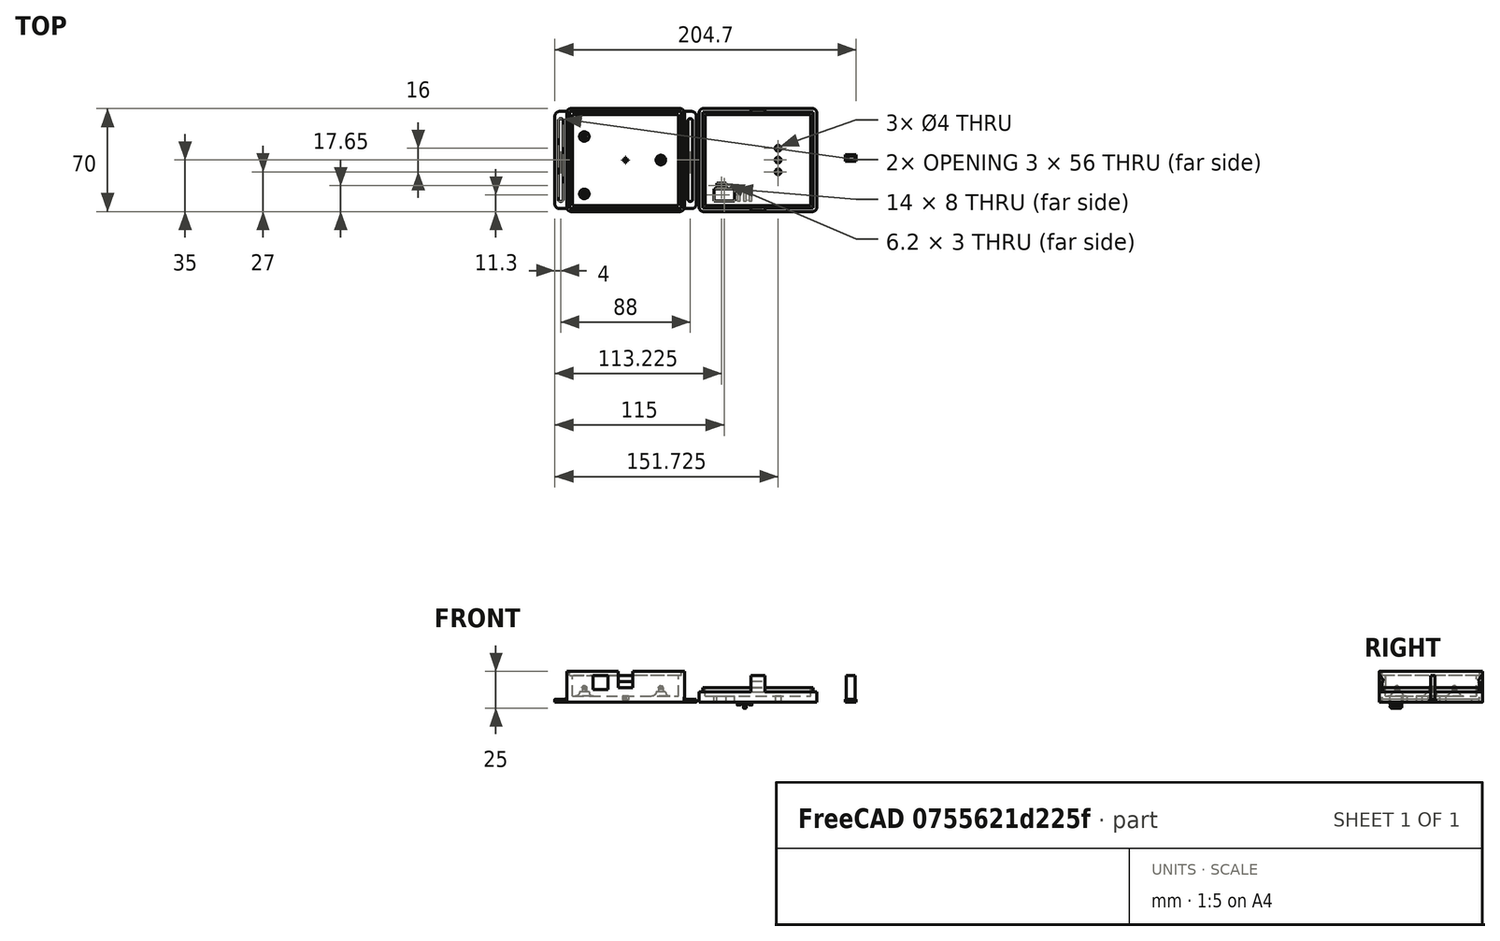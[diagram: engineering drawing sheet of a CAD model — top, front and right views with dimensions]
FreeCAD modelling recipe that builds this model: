
FCSTD DOCUMENT  (FreeCAD 1.0R39109 (Git))
Label: case
License: All rights reserved
LicenseURL: https://en.wikipedia.org/wiki/All_rights_reserved
objects: Sketcher::SketchObject×28, PartDesign::Pad×19, PartDesign::Body×12, PartDesign::Boolean×8, PartDesign::Fillet×6, PartDesign::Pocket×6, App::Link×3, App::FeaturePython×3, PartDesign::Revolution×3, PartDesign::Thickness×2, Assembly::JointGroup×1, Assembly::AssemblyObject×1, App::Part×1
note: 192 computed .brp shape members not serialized (recipe doc carries the construction recipe); baked Part::Feature solids carry a one-line shape summary decoded from their .brp

FEATURE [Sketcher::SketchObject] Sketch
  ArcFitTolerance = 1e-06
  AttachmentSupport = -> [XY_Plane001]
  FullyConstrained = true
  MakeInternals = false
  MapMode = 5
  sketch-geometry (4):
    g0: LineSegment StartX=-40 StartY=35 StartZ=0 EndX=-40 EndY=-35 EndZ=0
    g1: LineSegment StartX=-40 StartY=-35 StartZ=0 EndX=40 EndY=-35 EndZ=0
    g2: LineSegment StartX=40 StartY=-35 StartZ=0 EndX=40 EndY=35 EndZ=0
    g3: LineSegment StartX=40 StartY=35 StartZ=0 EndX=-40 EndY=35 EndZ=0
  constraints (10):
    c: Coincident(g0,g1)
    c: Coincident(g1,g2)
    c: Coincident(g2,g3)
    c: Coincident(g3,g0)
    c: Vertical(g2)
    c: Horizontal(g1)
    c: Symmetric(g0,g2,g-2)
    c: Symmetric(g0,g0,g-1)
    c: DistanceX(g3,g3) = 80
    c: DistanceY(g2,g2) = 70
FEATURE [PartDesign::Pad] Pad  label="case"
  Direction = (0,0,1)
  Length = 21
  Length2 = 10
  Profile = -> Sketch
  ReferenceAxis = -> Sketch [N_Axis]
  Refine = true
  Suppressed = false
  Type = 0
FEATURE [PartDesign::Thickness] Thickness  label="case_t"
  Base = -> Pad [Face6]
  BaseFeature = -> Pad
  Intersection = false
  Join = 0
  Mode = 0
  Refine = true
  Reversed = true
  SupportTransform = false
  Suppressed = false
  Value = 4
FEATURE [PartDesign::Fillet] Fillet
  Base = -> Thickness [Edge1,Edge2,Edge5,Edge8]
  BaseFeature = -> Thickness
  Radius = 3
  Refine = true
  SupportTransform = false
  Suppressed = false
  UseAllEdges = false
FEATURE [Sketcher::SketchObject] Sketch001  label="pcb_holders_s"
  ArcFitTolerance = 1e-06
  AttachmentSupport = -> [Fillet]
  FullyConstrained = true
  MakeInternals = false
  MapMode = 5
  Placement = pos=(0,0,4) rot=(0,0,1;0rad)
  sketch-geometry (7):
    g0: Circle CenterX=-28 CenterY=-23 CenterZ=0 NormalX=0 NormalY=0 NormalZ=1 AngleXU=0 Radius=3.25
    g1: Circle CenterX=-28 CenterY=16 CenterZ=0 NormalX=0 NormalY=0 NormalZ=1 AngleXU=0 Radius=3.25
    g2: Circle CenterX=24 CenterY=-1.1e-15 CenterZ=0 NormalX=0 NormalY=0 NormalZ=1 AngleXU=0 Radius=3.25
    g3: LineSegment [constr] StartX=-32 StartY=27 StartZ=0 EndX=-32 EndY=-27 EndZ=0
    g4: LineSegment [constr] StartX=-32 StartY=-27 StartZ=0 EndX=32 EndY=-27 EndZ=0
    g5: LineSegment [constr] StartX=32 StartY=-27 StartZ=0 EndX=32 EndY=27 EndZ=0
    g6: LineSegment [constr] StartX=32 StartY=27 StartZ=0 EndX=-32 EndY=27 EndZ=0
  constraints (19):
    c: Radius(g0) = 3.25
    c: Radius(g1) = 3.25
    c: Diameter(g2) = 6.5
    c: Coincident(g3,g4)
    c: Coincident(g4,g5)
    c: Coincident(g5,g6)
    c: Coincident(g6,g3)
    c: Vertical(g3)
    c: Horizontal(g6)
    c: DistanceX(g6,g6) = 64
    c: DistanceY(g3,g3) = 54
    c: Symmetric(g3,g4,g-2)
    c: Symmetric(g5,g4,g-1)
    c: Distance(g0,g4) = 4
    c: Distance(g0,g3) = 4
    c: Distance(g1,g3) = 4
    c: Distance(g1,g6) = 11
    c: Distance(g2,g5) = 8
    c: Distance(g2,g4) = 27
FEATURE [PartDesign::Pad] Pad001  label="pcb_holders_p"
  BaseFeature = -> Fillet
  Direction = (0,0,1)
  Length = 3
  Length2 = 10
  Profile = -> Sketch001
  ReferenceAxis = -> Sketch001 [N_Axis]
  Refine = true
  Suppressed = false
  Type = 0
FEATURE [PartDesign::Fillet] Fillet001  label="pcb_holder_f"
  Base = -> Pad001 [Edge39,Edge38,Edge37]
  BaseFeature = -> Pad001
  Radius = 2.99
  Refine = true
  SupportTransform = false
  Suppressed = false
  UseAllEdges = false
FEATURE [Sketcher::SketchObject] Sketch003  label="barreljack_window_s"
  ArcFitTolerance = 1e-06
  AttachmentOffset = pos=(0,0,8.55) rot=(0,0,1;0rad)
  AttachmentSupport = -> [XY_Plane001]
  FullyConstrained = true
  MakeInternals = false
  MapMode = 5
  Placement = pos=(0,0,8.55) rot=(0,0,1;0rad)
  sketch-geometry (8):
    g0: LineSegment [constr] StartX=-32 StartY=27 StartZ=0 EndX=-32 EndY=-27 EndZ=0
    g1: LineSegment [constr] StartX=-32 StartY=-27 StartZ=0 EndX=32 EndY=-27 EndZ=0
    g2: LineSegment [constr] StartX=32 StartY=-27 StartZ=0 EndX=32 EndY=27 EndZ=0
    g3: LineSegment [constr] StartX=32 StartY=27 StartZ=0 EndX=-32 EndY=27 EndZ=0
    g4: LineSegment StartX=-22 StartY=-20 StartZ=0 EndX=-22 EndY=-36 EndZ=0
    g5: LineSegment StartX=-22 StartY=-36 StartZ=0 EndX=-12 EndY=-36 EndZ=0
    g6: LineSegment StartX=-12 StartY=-36 StartZ=0 EndX=-12 EndY=-20 EndZ=0
    g7: LineSegment StartX=-12 StartY=-20 StartZ=0 EndX=-22 EndY=-20 EndZ=0
  constraints (22):
    c: Coincident(g0,g1)
    c: Coincident(g1,g2)
    c: Coincident(g2,g3)
    c: Coincident(g3,g0)
    c: Vertical(g2)
    c: Horizontal(g1)
    c: Distance(g0,g2) = 64
    c: Distance(g1,g3) = 54
    c: Symmetric(g0,g2,g-2)
    c: Symmetric(g0,g0,g-1)
    c: Coincident(g4,g5)
    c: Coincident(g5,g6)
    c: Coincident(g6,g7)
    c: Coincident(g7,g4)
    c: Vertical(g4)
    c: Vertical(g6)
    c: Horizontal(g5)
    c: Horizontal(g7)
    c: Distance(g0,g4) = 10
    c: DistanceX(g7,g7) = 10
    c: DistanceY(g6,g6) = 16
    c: Distance(g1,g7) = 7
FEATURE [PartDesign::Pocket] Pocket  label="barreljack_window_p"
  BaseFeature = -> Fillet001
  Direction = (0,0,-1)
  Length = 9.5
  Length2 = 5
  Profile = -> Sketch003
  ReferenceAxis = -> Sketch003 [N_Axis]
  Refine = true
  Reversed = true
  Suppressed = false
  Type = 0
FEATURE [Sketcher::SketchObject] Sketch004  label="fitting_s001"
  ArcFitTolerance = 1e-06
  AttachmentOffset = pos=(0,0,18) rot=(0,0,1;0rad)
  AttachmentSupport = -> [XY_Plane001]
  ExternalGeometry = -> [Pocket]
  FullyConstrained = true
  MakeInternals = false
  MapMode = 5
  Placement = pos=(0,0,18) rot=(0,0,1;0rad)
  sketch-geometry (4):
    g0: LineSegment StartX=-38 StartY=33 StartZ=0 EndX=-38 EndY=-33 EndZ=0
    g1: LineSegment StartX=-38 StartY=-33 StartZ=0 EndX=38 EndY=-33 EndZ=0
    g2: LineSegment StartX=38 StartY=-33 StartZ=0 EndX=38 EndY=33 EndZ=0
    g3: LineSegment StartX=38 StartY=33 StartZ=0 EndX=-38 EndY=33 EndZ=0
  constraints (12):
    c: Coincident(g0,g1)
    c: Coincident(g1,g2)
    c: Coincident(g2,g3)
    c: Coincident(g3,g0)
    c: Vertical(g0)
    c: Vertical(g2)
    c: Horizontal(g1)
    c: Horizontal(g3)
    c: DistanceX(g0,g-4) = 2
    c: DistanceY(g-4,g0) = 2
    c: DistanceY(g1,g-6) = 2
    c: DistanceX(g-6,g1) = 2
FEATURE [PartDesign::Pocket] Pocket001  label="fitting_p001"
  BaseFeature = -> Pocket
  Direction = (0,0,-1)
  Length = 5
  Length2 = 5
  Profile = -> Sketch004
  ReferenceAxis = -> Sketch004 [N_Axis]
  Refine = true
  Reversed = true
  Suppressed = false
  Type = 0
FEATURE [Sketcher::SketchObject] Sketch005  label="case_s"
  ArcFitTolerance = 1e-06
  AttachmentSupport = -> [XY_Plane002]
  FullyConstrained = true
  MakeInternals = false
  MapMode = 5
  sketch-geometry (4):
    g0: LineSegment StartX=-40 StartY=35 StartZ=0 EndX=-40 EndY=-35 EndZ=0
    g1: LineSegment StartX=-40 StartY=-35 StartZ=0 EndX=40 EndY=-35 EndZ=0
    g2: LineSegment StartX=40 StartY=-35 StartZ=0 EndX=40 EndY=35 EndZ=0
    g3: LineSegment StartX=40 StartY=35 StartZ=0 EndX=-40 EndY=35 EndZ=0
  constraints (10):
    c: Coincident(g0,g1)
    c: Coincident(g1,g2)
    c: Coincident(g2,g3)
    c: Coincident(g3,g0)
    c: Vertical(g2)
    c: Horizontal(g1)
    c: Symmetric(g0,g2,g-2)
    c: Symmetric(g0,g0,g-1)
    c: DistanceX(g3,g3) = 80
    c: DistanceY(g2,g2) = 70
FEATURE [PartDesign::Pad] Pad003  label="case_p"
  Direction = (0,0,1)
  Length = 10
  Length2 = 10
  Profile = -> Sketch005
  ReferenceAxis = -> Sketch005 [N_Axis]
  Refine = true
  Suppressed = false
  Type = 0
FEATURE [PartDesign::Thickness] Thickness001  label="case_t001"
  Base = -> Pad003 [Face6]
  BaseFeature = -> Pad003
  Intersection = false
  Join = 0
  Mode = 0
  Refine = true
  Reversed = true
  SupportTransform = false
  Suppressed = false
  Value = 4
FEATURE [PartDesign::Fillet] Fillet002
  Base = -> Thickness001 [Edge2,Edge1,Edge5,Edge8]
  BaseFeature = -> Thickness001
  Radius = 3
  Refine = true
  SupportTransform = false
  Suppressed = false
  UseAllEdges = false
FEATURE [Sketcher::SketchObject] Sketch008  label="fitting_s"
  ArcFitTolerance = 1e-06
  AttachmentOffset = pos=(0,0,7) rot=(0,0,1;0rad)
  AttachmentSupport = -> [XY_Plane002]
  FullyConstrained = true
  MakeInternals = false
  MapMode = 5
  Placement = pos=(0,0,7) rot=(0,0,1;0rad)
  sketch-geometry (20):
    g0: LineSegment StartX=-42.5 StartY=50 StartZ=0 EndX=-42.5 EndY=-50 EndZ=0
    g1: LineSegment StartX=-42.5 StartY=-50 StartZ=0 EndX=-37.5 EndY=-50 EndZ=0
    g2: LineSegment StartX=-37.5 StartY=-50 StartZ=0 EndX=-37.5 EndY=50 EndZ=0
    g3: LineSegment StartX=-37.5 StartY=50 StartZ=0 EndX=-42.5 EndY=50 EndZ=0
    g4: LineSegment StartX=-50 StartY=37.5 StartZ=0 EndX=-50 EndY=32.5 EndZ=0
    g5: LineSegment StartX=-50 StartY=32.5 StartZ=0 EndX=50 EndY=32.5 EndZ=0
    g6: LineSegment StartX=50 StartY=32.5 StartZ=0 EndX=50 EndY=37.5 EndZ=0
    g7: LineSegment StartX=50 StartY=37.5 StartZ=0 EndX=-50 EndY=37.5 EndZ=0
    g8: LineSegment StartX=37.5 StartY=50 StartZ=0 EndX=37.5 EndY=-50 EndZ=0
    g9: LineSegment StartX=37.5 StartY=-50 StartZ=0 EndX=42.5 EndY=-50 EndZ=0
    g10: LineSegment StartX=42.5 StartY=-50 StartZ=0 EndX=42.5 EndY=50 EndZ=0
    g11: LineSegment StartX=42.5 StartY=50 StartZ=0 EndX=37.5 EndY=50 EndZ=0
    g12: LineSegment StartX=50 StartY=-37.5 StartZ=0 EndX=50 EndY=-32.5 EndZ=0
    g13: LineSegment StartX=50 StartY=-32.5 StartZ=0 EndX=-50 EndY=-32.5 EndZ=0
    g14: LineSegment StartX=-50 StartY=-32.5 StartZ=0 EndX=-50 EndY=-37.5 EndZ=0
    g15: LineSegment StartX=-50 StartY=-37.5 StartZ=0 EndX=50 EndY=-37.5 EndZ=0
    g16: LineSegment [constr] StartX=-40 StartY=35 StartZ=0 EndX=-40 EndY=-35 EndZ=0
    g17: LineSegment [constr] StartX=-40 StartY=-35 StartZ=0 EndX=40 EndY=-35 EndZ=0
    g18: LineSegment [constr] StartX=40 StartY=-35 StartZ=0 EndX=40 EndY=35 EndZ=0
    g19: LineSegment [constr] StartX=40 StartY=35 StartZ=0 EndX=-40 EndY=35 EndZ=0
  constraints (54):
    c: Coincident(g0,g1)
    c: Coincident(g1,g2)
    c: Coincident(g2,g3)
    c: Coincident(g3,g0)
    c: Vertical(g2)
    c: Horizontal(g1)
    c: Horizontal(g3)
    c: Coincident(g4,g5)
    c: Coincident(g5,g6)
    c: Coincident(g6,g7)
    c: Coincident(g7,g4)
    c: Vertical(g4)
    c: Vertical(g6)
    c: Horizontal(g5)
    c: Coincident(g8,g9)
    c: Coincident(g9,g10)
    c: Coincident(g10,g11)
    c: Coincident(g11,g8)
    c: Vertical(g8)
    c: Horizontal(g9)
    c: Horizontal(g11)
    c: Coincident(g12,g13)
    c: Coincident(g13,g14)
    c: Coincident(g14,g15)
    c: Coincident(g15,g12)
    c: Vertical(g12)
    c: Vertical(g14)
    c: Horizontal(g15)
    c: DistanceY(g14,g14) = 5
    c: DistanceX(g9,g9) = 5
    c: DistanceY(g6,g6) = 5
    c: DistanceX(g1,g1) = 5
    c: Symmetric(g0,g0,g-1)
    c: Symmetric(g10,g9,g-1)
    c: Symmetric(g13,g12,g-2)
    c: Symmetric(g4,g6,g-2)
    c: DistanceX(g7,g7) = 100
    c: DistanceY(g0,g0) = 100
    c: DistanceY(g10,g10) = 100
    c: DistanceX(g15,g15) = 100
    c: Coincident(g16,g17)
    c: Coincident(g17,g18)
    c: Coincident(g18,g19)
    c: Coincident(g19,g16)
    c: Vertical(g18)
    c: Horizontal(g19)
    c: Distance(g16,g18) = 80
    c: Distance(g17,g19) = 70
    c: Symmetric(g16,g16,g-1)
    c: Symmetric(g16,g17,g-2)
    c: DistanceX(g16,g2) = 2.5
    c: DistanceX(g8,g18) = 2.5
    c: DistanceY(g4,g16) = 2.5
    c: DistanceY(g16,g13) = 2.5
FEATURE [PartDesign::Pocket] Pocket002  label="fitting_p"
  BaseFeature = -> Fillet002
  Direction = (0,0,-1)
  Length = 5
  Length2 = 5
  Profile = -> Sketch008
  ReferenceAxis = -> Sketch008 [N_Axis]
  Refine = true
  Reversed = true
  Suppressed = false
  Type = 0
FEATURE [Sketcher::SketchObject] Sketch009  label="top_holes_sk"
  ArcFitTolerance = 1e-06
  AttachmentOffset = pos=(0,-1,0) rot=(0,0,1;0rad)
  AttachmentSupport = -> [XY_Plane002]
  FullyConstrained = true
  MakeInternals = false
  MapMode = 5
  Placement = pos=(0,-1,0) rot=(0,0,1;0rad)
  sketch-geometry (15):
    g0: LineSegment [constr] StartX=-32 StartY=27 StartZ=0 EndX=-32 EndY=-27 EndZ=0
    g1: LineSegment [constr] StartX=-32 StartY=-27 StartZ=0 EndX=32 EndY=-27 EndZ=0
    g2: LineSegment [constr] StartX=32 StartY=-27 StartZ=0 EndX=32 EndY=27 EndZ=0
    g3: LineSegment [constr] StartX=32 StartY=27 StartZ=0 EndX=-32 EndY=27 EndZ=0
    g4: LineSegment StartX=-30 StartY=-18.7 StartZ=0 EndX=-30 EndY=-26.7 EndZ=0
    g5: LineSegment StartX=-30 StartY=-26.7 StartZ=0 EndX=-16 EndY=-26.7 EndZ=0
    g6: LineSegment StartX=-16 StartY=-26.7 StartZ=0 EndX=-16 EndY=-18.7 EndZ=0
    g7: LineSegment StartX=-16 StartY=-18.7 StartZ=0 EndX=-30 EndY=-18.7 EndZ=0
    g8: LineSegment StartX=-27.875 StartY=-14.85 StartZ=0 EndX=-27.875 EndY=-17.85 EndZ=0
    g9: LineSegment StartX=-27.875 StartY=-17.85 StartZ=0 EndX=-21.675 EndY=-17.85 EndZ=0
    g10: LineSegment StartX=-21.675 StartY=-17.85 StartZ=0 EndX=-21.675 EndY=-14.85 EndZ=0
    g11: LineSegment StartX=-21.675 StartY=-14.85 StartZ=0 EndX=-27.875 EndY=-14.85 EndZ=0
    g12: Circle CenterX=13.725 CenterY=9 CenterZ=0 NormalX=0 NormalY=0 NormalZ=1 AngleXU=0 Radius=2
    g13: Circle CenterX=13.725 CenterY=1 CenterZ=0 NormalX=0 NormalY=0 NormalZ=1 AngleXU=0 Radius=2
    g14: Circle CenterX=13.725 CenterY=-7 CenterZ=0 NormalX=0 NormalY=0 NormalZ=1 AngleXU=0 Radius=2
  constraints (43):
    c: Coincident(g0,g1)
    c: Coincident(g1,g2)
    c: Coincident(g2,g3)
    c: Coincident(g3,g0)
    c: Vertical(g2)
    c: Horizontal(g1)
    c: Distance(g0,g2) = 64
    c: Distance(g1,g3) = 54
    c: Symmetric(g0,g2,g-2)
    c: Symmetric(g0,g0,g-1)
    c: Coincident(g4,g5)
    c: Coincident(g5,g6)
    c: Coincident(g6,g7)
    c: Coincident(g7,g4)
    c: Vertical(g4)
    c: Vertical(g6)
    c: Horizontal(g5)
    c: Horizontal(g7)
    c: Coincident(g8,g9)
    c: Coincident(g9,g10)
    c: Coincident(g10,g11)
    c: Coincident(g11,g8)
    c: Vertical(g8)
    c: Vertical(g10)
    c: Horizontal(g9)
    c: Horizontal(g11)
    c: Distance(g0,g4) = 2
    c: Distance(g1,g5) = 0.3
    c: DistanceX(g7,g7) = 14
    c: DistanceY(g4,g4) = 8
    c: Distance(g1,g9) = 9.15
    c: Distance(g0,g8) = 4.125
    c: DistanceX(g11,g11) = 6.2
    c: DistanceY(g10,g10) = 3
    c: Diameter(g12) = 4
    c: Equal(g12,g13)
    c: Equal(g13,g14)
    c: Distance(g12,g2) = 18.275
    c: Distance(g13,g2) = 18.275
    c: Distance(g14,g2) = 18.275
    c: Distance(g12,g3) = 18
    c: DistanceY(g13,g12) = 8
    c: DistanceY(g14,g13) = 8
FEATURE [PartDesign::Pocket] Pocket004  label="top_holes_p"
  BaseFeature = -> Pocket002
  Direction = (0,0,-1)
  Length = 5
  Length2 = 5
  Profile = -> Sketch009
  ReferenceAxis = -> Sketch009 [N_Axis]
  Refine = true
  Reversed = true
  Suppressed = false
  Type = 1
FEATURE [Sketcher::SketchObject] Sketch014
  ArcFitTolerance = 1e-06
  AttachmentSupport = -> [XY_Plane005]
  FullyConstrained = true
  MakeInternals = false
  MapMode = 5
  sketch-geometry (4):
    g0: LineSegment StartX=0 StartY=2.7 StartZ=0 EndX=0 EndY=0 EndZ=0
    g1: LineSegment StartX=0 StartY=0 StartZ=0 EndX=5.9 EndY=0 EndZ=0
    g2: LineSegment StartX=5.9 StartY=0 StartZ=0 EndX=5.9 EndY=2.7 EndZ=0
    g3: LineSegment StartX=5.9 StartY=2.7 StartZ=0 EndX=0 EndY=2.7 EndZ=0
  constraints (11):
    c: Coincident(g0,g1)
    c: Coincident(g1,g2)
    c: Coincident(g2,g3)
    c: Coincident(g3,g0)
    c: Vertical(g0)
    c: Vertical(g2)
    c: Horizontal(g1)
    c: Horizontal(g3)
    c: Distance(g0,g2) = 5.9
    c: Distance(g1,g3) = 2.7
    c: Coincident(g0,g-1)
FEATURE [PartDesign::Pad] Pad006
  Direction = (0,0,1)
  Length = 18
  Length2 = 10
  Profile = -> Sketch014
  ReferenceAxis = -> Sketch014 [N_Axis]
  Refine = true
  Suppressed = false
  Type = 0
FEATURE [Sketcher::SketchObject] Sketch015
  ArcFitTolerance = 1e-06
  AttachmentSupport = -> [XY_Plane005]
  ExternalGeometry = -> [Sketch014]
  FullyConstrained = true
  MakeInternals = false
  MapMode = 5
  sketch-geometry (4):
    g0: LineSegment StartX=-0.8 StartY=3.5 StartZ=0 EndX=-0.8 EndY=-0.8 EndZ=0
    g1: LineSegment StartX=-0.8 StartY=-0.8 StartZ=0 EndX=6.7 EndY=-0.8 EndZ=0
    g2: LineSegment StartX=6.7 StartY=-0.8 StartZ=0 EndX=6.7 EndY=3.5 EndZ=0
    g3: LineSegment StartX=6.7 StartY=3.5 StartZ=0 EndX=-0.8 EndY=3.5 EndZ=0
  constraints (12):
    c: Coincident(g0,g1)
    c: Coincident(g1,g2)
    c: Coincident(g2,g3)
    c: Coincident(g3,g0)
    c: Vertical(g0)
    c: Vertical(g2)
    c: Horizontal(g1)
    c: Horizontal(g3)
    c: Distance(g-3,g3) = 0.8
    c: Distance(g2,g-4) = 0.8
    c: Distance(g-3,g0) = 0.8
    c: Distance(g-4,g1) = 0.8
FEATURE [PartDesign::Pad] Pad007
  BaseFeature = -> Pad006
  Direction = (0,0,1)
  Length = 2
  Length2 = 10
  Profile = -> Sketch015
  ReferenceAxis = -> Sketch015 [N_Axis]
  Refine = true
  Suppressed = false
  Type = 0
FEATURE [PartDesign::Body] Body004  label="button_b"
  AllowCompound = false
  Group = -> [Sketch014,Pad006,Sketch015,Pad007]
  Origin = -> Origin005
  Placement = pos=(150,0,0) rot=(0,0,1;0rad)
  Tip = -> Pad007
FEATURE [Sketcher::SketchObject] Sketch018  label="holders_s"
  ArcFitTolerance = 1e-06
  AttachmentSupport = -> [XY_Plane001]
  FullyConstrained = true
  MakeInternals = false
  MapMode = 5
  sketch-geometry (40):
    g0: LineSegment StartX=-38 StartY=33 StartZ=0 EndX=-45 EndY=33 EndZ=0
    g1: LineSegment StartX=-48 StartY=30 StartZ=0 EndX=-48 EndY=-30 EndZ=0
    g2: LineSegment StartX=-45 StartY=-33 StartZ=0 EndX=-38 EndY=-33 EndZ=0
    g3: LineSegment StartX=-38 StartY=-33 StartZ=0 EndX=-38 EndY=33 EndZ=0
    g4: LineSegment StartX=38 StartY=33 StartZ=0 EndX=38 EndY=-33 EndZ=0
    g5: LineSegment StartX=38 StartY=-33 StartZ=0 EndX=45 EndY=-33 EndZ=0
    g6: LineSegment StartX=48 StartY=-30 StartZ=0 EndX=48 EndY=30 EndZ=0
    g7: LineSegment StartX=45 StartY=33 StartZ=0 EndX=38 EndY=33 EndZ=0
    g8: ArcOfCircle CenterX=-45 CenterY=30 CenterZ=0 NormalX=0 NormalY=0 NormalZ=1 AngleXU=0 Radius=3 StartAngle=1.5708 EndAngle=3.14159
    g9: GeomPoint [constr] X=-48 Y=33 Z=0
    g10: ArcOfCircle CenterX=-45 CenterY=-30 CenterZ=0 NormalX=0 NormalY=0 NormalZ=1 AngleXU=0 Radius=3 StartAngle=3.14159 EndAngle=4.71239
    g11: GeomPoint [constr] X=-48 Y=-33 Z=0
    g12: ArcOfCircle CenterX=45 CenterY=30 CenterZ=0 NormalX=0 NormalY=0 NormalZ=1 AngleXU=0 Radius=3 StartAngle=2e-16 EndAngle=1.5708
    g13: GeomPoint [constr] X=48 Y=33 Z=0
    g14: ArcOfCircle CenterX=45 CenterY=-30 CenterZ=0 NormalX=0 NormalY=0 NormalZ=1 AngleXU=0 Radius=3 StartAngle=4.71239 EndAngle=6.28319
    g15: GeomPoint [constr] X=48 Y=-33 Z=0
    g16: LineSegment StartX=-45.5 StartY=27 StartZ=0 EndX=-45.5 EndY=-27 EndZ=0
    g17: LineSegment StartX=-44.5 StartY=-28 StartZ=0 EndX=-43.5 EndY=-28 EndZ=0
    g18: LineSegment StartX=-42.5 StartY=-27 StartZ=0 EndX=-42.5 EndY=27 EndZ=0
    g19: LineSegment StartX=-43.5 StartY=28 StartZ=0 EndX=-44.5 EndY=28 EndZ=0
    g20: LineSegment StartX=42.5 StartY=27 StartZ=0 EndX=42.5 EndY=-27 EndZ=0
    g21: LineSegment StartX=43.5 StartY=-28 StartZ=0 EndX=44.5 EndY=-28 EndZ=0
    g22: LineSegment StartX=45.5 StartY=-27 StartZ=0 EndX=45.5 EndY=27 EndZ=0
    g23: LineSegment StartX=44.5 StartY=28 StartZ=0 EndX=43.5 EndY=28 EndZ=0
    g24: ArcOfCircle CenterX=-44.5 CenterY=27 CenterZ=0 NormalX=0 NormalY=0 NormalZ=1 AngleXU=0 Radius=1 StartAngle=1.5708 EndAngle=3.14159
    g25: GeomPoint [constr] X=-45.5 Y=28 Z=0
    g26: ArcOfCircle CenterX=-43.5 CenterY=27 CenterZ=0 NormalX=0 NormalY=0 NormalZ=1 AngleXU=0 Radius=1 StartAngle=1.7e-15 EndAngle=1.5708
    g27: GeomPoint [constr] X=-42.5 Y=28 Z=0
    g28: ArcOfCircle CenterX=-44.5 CenterY=-27 CenterZ=0 NormalX=0 NormalY=0 NormalZ=1 AngleXU=0 Radius=1 StartAngle=3.14159 EndAngle=4.71239
    g29: GeomPoint [constr] X=-45.5 Y=-28 Z=0
    g30: ArcOfCircle CenterX=-43.5 CenterY=-27 CenterZ=0 NormalX=0 NormalY=0 NormalZ=1 AngleXU=0 Radius=1 StartAngle=4.71239 EndAngle=6.28319
    g31: GeomPoint [constr] X=-42.5 Y=-28 Z=0
    g32: ArcOfCircle CenterX=43.5 CenterY=-27 CenterZ=0 NormalX=0 NormalY=0 NormalZ=1 AngleXU=0 Radius=1 StartAngle=3.14159 EndAngle=4.71239
    g33: GeomPoint [constr] X=42.5 Y=-28 Z=0
    g34: ArcOfCircle CenterX=44.5 CenterY=-27 CenterZ=0 NormalX=0 NormalY=0 NormalZ=1 AngleXU=0 Radius=1 StartAngle=4.71239 EndAngle=6.28319
    g35: GeomPoint [constr] X=45.5 Y=-28 Z=0
    g36: ArcOfCircle CenterX=43.5 CenterY=27 CenterZ=0 NormalX=0 NormalY=0 NormalZ=1 AngleXU=0 Radius=1 StartAngle=1.5708 EndAngle=3.14159
    g37: GeomPoint [constr] X=42.5 Y=28 Z=0
    g38: ArcOfCircle CenterX=44.5 CenterY=27 CenterZ=0 NormalX=0 NormalY=0 NormalZ=1 AngleXU=0 Radius=1 StartAngle=-5.7785e-12 EndAngle=1.5708
    g39: GeomPoint [constr] X=45.5 Y=28 Z=0
  constraints (94):
    c: Coincident(g2,g3)
    c: Coincident(g3,g0)
    c: Horizontal(g0)
    c: Horizontal(g2)
    c: Vertical(g1)
    c: Vertical(g3)
    c: Distance(g9,g3) = 10
    c: Distance(g0,g2) = 66
    c: Coincident(g0,g-3)
    c: Coincident(g4,g5)
    c: Coincident(g7,g4)
    c: Vertical(g4)
    c: Vertical(g6)
    c: Horizontal(g5)
    c: Horizontal(g7)
    c: Distance(g4,g13) = 10
    c: Distance(g5,g7) = 66
    c: Coincident(g4,g-4)
    c: PointOnObject(g9,g0)
    c: PointOnObject(g9,g1)
    c: Tangent(g0,g8) = -1.5708
    c: Tangent(g1,g8) = -1.5708
    c: PointOnObject(g11,g1)
    c: PointOnObject(g11,g2)
    c: Tangent(g1,g10) = -1.5708
    c: Tangent(g2,g10) = -1.5708
    c: PointOnObject(g13,g7)
    c: PointOnObject(g13,g6)
    c: Tangent(g7,g12) = -1.5708
    c: Tangent(g6,g12) = -1.5708
    c: PointOnObject(g15,g5)
    c: PointOnObject(g15,g6)
    c: Tangent(g5,g14) = -1.5708
    c: Tangent(g6,g14) = -1.5708
    c: Radius(g8) = 3
    c: Radius(g10) = 3
    c: Radius(g14) = 3
    c: Radius(g12) = 3
    c: Vertical(g16)
    c: Vertical(g18)
    c: Horizontal(g17)
    c: Horizontal(g19)
    c: Distance(g25,g27) = 3
    c: Distance(g29,g25) = 56
    c: Distance(g3,g18) = 4.5
    c: Vertical(g20)
    c: Vertical(g22)
    c: Horizontal(g21)
    c: Horizontal(g23)
    c: Distance(g37,g39) = 3
    c: Distance(g33,g37) = 56
    c: Distance(g4,g20) = 4.5
    c: Distance(g27,g0) = 5
    c: Distance(g39,g7) = 5
    c: PointOnObject(g25,g19)
    c: PointOnObject(g25,g16)
    c: Tangent(g19,g24) = -1.5708
    c: Tangent(g16,g24) = -1.5708
    c: PointOnObject(g27,g19)
    c: PointOnObject(g27,g18)
    c: Tangent(g19,g26) = -1.5708
    c: Tangent(g18,g26) = -1.5708
    c: PointOnObject(g29,g17)
    c: PointOnObject(g29,g16)
    c: Tangent(g17,g28) = -1.5708
    c: Tangent(g16,g28) = -1.5708
    c: PointOnObject(g31,g17)
    c: PointOnObject(g31,g18)
    c: Tangent(g17,g30) = -1.5708
    c: Tangent(g18,g30) = -1.5708
    c: PointOnObject(g33,g20)
    c: PointOnObject(g33,g21)
    c: Tangent(g20,g32) = -1.5708
    c: Tangent(g21,g32) = -1.5708
    c: PointOnObject(g35,g22)
    c: PointOnObject(g35,g21)
    c: Tangent(g22,g34) = -1.5708
    c: Tangent(g21,g34) = -1.5708
    c: PointOnObject(g37,g23)
    c: PointOnObject(g37,g20)
    c: Tangent(g23,g36) = -1.5708
    c: Tangent(g20,g36) = -1.5708
    c: PointOnObject(g39,g23)
    c: PointOnObject(g39,g22)
    c: Tangent(g23,g38) = -1.5708
    c: Tangent(g22,g38) = -1.5708
    c: Radius(g24) = 1
    c: Radius(g26) = 1
    c: Radius(g28) = 1
    c: Radius(g30) = 1
    c: Radius(g32) = 1
    c: Radius(g34) = 1
    c: Radius(g36) = 1
    c: Radius(g38) = 1
FEATURE [PartDesign::Pad] Pad009  label="holders_p"
  BaseFeature = -> Pocket001
  Direction = (0,0,1)
  Length = 2
  Length2 = 10
  Profile = -> Sketch018
  ReferenceAxis = -> Sketch018 [N_Axis]
  Refine = true
  Suppressed = false
  Type = 0
FEATURE [PartDesign::Fillet] Fillet004  label="holders_f"
  Base = -> Pad009 [Edge77,Edge89]
  BaseFeature = -> Pad009
  Radius = 1.5
  Refine = true
  SupportTransform = false
  Suppressed = false
  UseAllEdges = false
FEATURE [Sketcher::SketchObject] Sketch016  label="clips_holders_s"
  ArcFitTolerance = 1e-06
  AttachmentSupport = -> [YZ_Plane001]
  ExternalGeometry = -> [Pad]
  FullyConstrained = true
  MakeInternals = false
  MapMode = 5
  Placement = pos=(0,0,0) rot=(0.57735,0.57735,0.57735;2.0944rad)
  sketch-geometry (10):
    g0: LineSegment StartX=33 StartY=18 StartZ=0 EndX=35 EndY=18 EndZ=0
    g1: LineSegment StartX=35 StartY=18 StartZ=0 EndX=35 EndY=9.9 EndZ=0
    g2: LineSegment StartX=35 StartY=9.9 StartZ=0 EndX=31.9 EndY=14.1 EndZ=0
    g3: LineSegment StartX=31.9 StartY=14.1 StartZ=0 EndX=33 EndY=14.1 EndZ=0
    g4: LineSegment StartX=33 StartY=14.1 StartZ=0 EndX=33 EndY=18 EndZ=0
    g5: LineSegment StartX=-33 StartY=18 StartZ=0 EndX=-35 EndY=18 EndZ=0
    g6: LineSegment StartX=-35 StartY=18 StartZ=0 EndX=-35 EndY=9.9 EndZ=0
    g7: LineSegment StartX=-35 StartY=9.9 StartZ=0 EndX=-31.9 EndY=14.1 EndZ=0
    g8: LineSegment StartX=-31.9 StartY=14.1 StartZ=0 EndX=-33 EndY=14.1 EndZ=0
    g9: LineSegment StartX=-33 StartY=14.1 StartZ=0 EndX=-33 EndY=18 EndZ=0
  constraints (30):
    c: Coincident(g0,g1)
    c: Vertical(g1)
    c: Coincident(g2,g3)
    c: Coincident(g3,g4)
    c: Coincident(g4,g0)
    c: Vertical(g4)
    c: Coincident(g7,g8)
    c: Coincident(g8,g9)
    c: Coincident(g9,g5)
    c: Horizontal(g5)
    c: Coincident(g6,g5)
    c: DistanceY(g6,g6) = 8.1
    c: DistanceY(g9,g9) = 3.9
    c: Vertical(g9)
    c: Horizontal(g8)
    c: Vertical(g6)
    c: DistanceX(g8,g8) = 1.1
    c: DistanceY(g1,g1) = 8.1
    c: Horizontal(g3)
    c: DistanceX(g0,g0) = 2
    c: DistanceY(g4,g4) = 3.9
    c: DistanceX(g3,g3) = 1.1
    c: Horizontal(g0)
    c: DistanceX(g5,g5) = 2
    c: DistanceY(g5,g-3) = 3
    c: PointOnObject(g5,g-4)
    c: DistanceY(g0,g-5) = 3
    c: PointOnObject(g0,g-5)
    c: Coincident(g2,g1)
    c: Coincident(g7,g6)
FEATURE [PartDesign::Pocket] Pocket007  label="clip_holders_p"
  BaseFeature = -> Fillet004
  Direction = (-1,0,0)
  Length = 10
  Length2 = 5
  Midplane = true
  Profile = -> Sketch016
  ReferenceAxis = -> Sketch016 [N_Axis]
  Refine = true
  Suppressed = false
  Type = 0
FEATURE [Sketcher::SketchObject] Sketch019  label="clip_holders_clearance_s"
  ArcFitTolerance = 1e-06
  AttachmentSupport = -> [YZ_Plane001]
  ExternalGeometry = -> [Pocket007]
  FullyConstrained = true
  MakeInternals = false
  MapMode = 5
  Placement = pos=(0,0,0) rot=(0.57735,0.57735,0.57735;2.0944rad)
  sketch-geometry (8):
    g0: LineSegment StartX=-33 StartY=21 StartZ=0 EndX=-35 EndY=21 EndZ=0
    g1: LineSegment StartX=-35 StartY=21 StartZ=0 EndX=-35 EndY=18 EndZ=0
    g2: LineSegment StartX=-35 StartY=18 StartZ=0 EndX=-33 EndY=18 EndZ=0
    g3: LineSegment StartX=-33 StartY=18 StartZ=0 EndX=-33 EndY=21 EndZ=0
    g4: LineSegment StartX=33 StartY=21 StartZ=0 EndX=33 EndY=18 EndZ=0
    g5: LineSegment StartX=33 StartY=18 StartZ=0 EndX=35 EndY=18 EndZ=0
    g6: LineSegment StartX=35 StartY=18 StartZ=0 EndX=35 EndY=21 EndZ=0
    g7: LineSegment StartX=35 StartY=21 StartZ=0 EndX=33 EndY=21 EndZ=0
  constraints (20):
    c: Coincident(g0,g1)
    c: Coincident(g1,g2)
    c: Coincident(g2,g3)
    c: Coincident(g3,g0)
    c: Horizontal(g0)
    c: Horizontal(g2)
    c: Vertical(g1)
    c: Vertical(g3)
    c: Coincident(g0,g-5)
    c: Coincident(g1,g-6)
    c: Coincident(g4,g5)
    c: Coincident(g5,g6)
    c: Coincident(g6,g7)
    c: Coincident(g7,g4)
    c: Vertical(g4)
    c: Vertical(g6)
    c: Horizontal(g5)
    c: Horizontal(g7)
    c: Coincident(g4,g-10)
    c: Coincident(g5,g-9)
FEATURE [PartDesign::Pocket] Pocket008  label="clip_holder_clearance_p"
  BaseFeature = -> Pocket007
  Direction = (-1,0,0)
  Length = 10
  Length2 = 5
  Midplane = true
  Profile = -> Sketch019
  ReferenceAxis = -> Sketch019 [N_Axis]
  Refine = true
  Suppressed = false
  Type = 0
FEATURE [Sketcher::SketchObject] Sketch020  label="clips_s"
  ArcFitTolerance = 1e-06
  AttachmentSupport = -> [YZ_Plane002]
  ExternalGeometry = -> [Pocket004]
  FullyConstrained = true
  MakeInternals = false
  MapMode = 5
  Placement = pos=(0,0,0) rot=(0.57735,0.57735,0.57735;2.0944rad)
  sketch-geometry (12):
    g0: LineSegment StartX=35 StartY=7 StartZ=0 EndX=35 EndY=18 EndZ=0
    g1: LineSegment StartX=35 StartY=18 StartZ=0 EndX=34.5 EndY=18 EndZ=0
    g2: LineSegment StartX=34.5 StartY=18 StartZ=0 EndX=32 EndY=14.15 EndZ=0
    g3: LineSegment StartX=32 StartY=14.15 StartZ=0 EndX=33 EndY=14.15 EndZ=0
    g4: LineSegment StartX=33 StartY=14.15 StartZ=0 EndX=33 EndY=7 EndZ=0
    g5: LineSegment StartX=33 StartY=7 StartZ=0 EndX=35 EndY=7 EndZ=0
    g6: LineSegment StartX=-35 StartY=7 StartZ=0 EndX=-35 EndY=18 EndZ=0
    g7: LineSegment StartX=-35 StartY=18 StartZ=0 EndX=-34.5 EndY=18 EndZ=0
    g8: LineSegment StartX=-34.5 StartY=18 StartZ=0 EndX=-32 EndY=14.15 EndZ=0
    g9: LineSegment StartX=-32 StartY=14.15 StartZ=0 EndX=-33 EndY=14.15 EndZ=0
    g10: LineSegment StartX=-33 StartY=14.15 StartZ=0 EndX=-33 EndY=7 EndZ=0
    g11: LineSegment StartX=-33 StartY=7 StartZ=0 EndX=-35 EndY=7 EndZ=0
  constraints (34):
    c: Coincident(g-4,g0)
    c: Vertical(g0)
    c: Coincident(g0,g1)
    c: Coincident(g1,g2)
    c: Coincident(g2,g3)
    c: Horizontal(g3)
    c: Coincident(g3,g4)
    c: Vertical(g4)
    c: Coincident(g4,g5)
    c: Coincident(g5,g0)
    c: Horizontal(g5)
    c: DistanceY(g0,g0) = 11
    c: Horizontal(g1)
    c: DistanceX(g5,g5) = 2
    c: DistanceX(g1,g1) = 0.5
    c: DistanceX(g3,g3) = 1
    c: DistanceY(g4,g4) = 7.15
    c: Coincident(g-5,g6)
    c: Vertical(g6)
    c: Coincident(g6,g7)
    c: Horizontal(g7)
    c: Coincident(g7,g8)
    c: Coincident(g8,g9)
    c: Coincident(g9,g10)
    c: Coincident(g10,g11)
    c: Coincident(g11,g6)
    c: DistanceY(g6,g6) = 11
    c: Horizontal(g11)
    c: Horizontal(g9)
    c: Vertical(g10)
    c: DistanceY(g10,g10) = 7.15
    c: DistanceX(g7,g7) = 0.5
    c: DistanceX(g9,g9) = 1
    c: DistanceX(g11,g11) = 2
FEATURE [PartDesign::Pad] Pad010  label="clips_p"
  BaseFeature = -> Pocket004
  Direction = (1,0,0)
  Length = 9.45
  Length2 = 10
  Midplane = true
  Profile = -> Sketch020
  ReferenceAxis = -> Sketch020 [N_Axis]
  Refine = true
  Suppressed = false
  Type = 0
FEATURE [App::Link] bottom_b  label="bottom_b001"
  LinkedObject = -> Body
FEATURE [App::FeaturePython] GroundedJoint  # Assembly grounded joint (typed FeaturePython)
  ObjectToGround = -> bottom_b
FEATURE [App::Link] top_b  label="top_b001"
  LinkPlacement = pos=(0.275,-70,32.4232) rot=(0,1,0;3.14159rad)
  LinkedObject = -> Body001
  Placement = pos=(0.275,-70,32.4232) rot=(0,1,0;3.14159rad)
FEATURE [App::Link] button_b  label="button_b001"
  LinkPlacement = pos=(21.95,-85.85,21.7935) rot=(0,0,1;0rad)
  LinkedObject = -> Body004
  Placement = pos=(21.95,-85.85,21.7935) rot=(0,0,1;0rad)
FEATURE [App::FeaturePython] Joint  label="Slider"  # Assembly joint (typed FeaturePython)
  Activated = true
  AngleMax = 0
  AngleMin = 0
  Detach1 = false
  Detach2 = false
  Distance = 0
  Distance2 = 0
  EnableAngleMax = false
  EnableAngleMin = false
  EnableLengthMax = false
  EnableLengthMin = false
  JointType = 3 (Slider)
  LengthMax = 0
  LengthMin = 0
  Offset2 = pos=(0,0,0) rot=(0,0,1;3.14159rad)
  Placement1 = pos=(-4.725,35,12.5) rot=(0,0,1;0rad)
  Placement2 = pos=(5,-35,15.45) rot=(1,0,0;3.14159rad)
  Reference1 = -> Assembly [top_b.Edge67,top_b.Edge67]
  Reference2 = -> Assembly [bottom_b.Edge27,bottom_b.Edge27]
FEATURE [App::FeaturePython] Joint001  label="Slider001"  # Assembly joint (typed FeaturePython)
  Activated = true
  AngleMax = 0
  AngleMin = 0
  Detach1 = false
  Detach2 = false
  Distance = 0
  Distance2 = 0
  EnableAngleMax = false
  EnableAngleMin = false
  EnableLengthMax = false
  EnableLengthMin = false
  JointType = 3 (Slider)
  LengthMax = 0
  LengthMin = 0
  Offset2 = pos=(0,0,0) rot=(0,0,1;3.14159rad)
  Placement1 = pos=(0,0,10) rot=(0,0,1;0rad)
  Placement2 = pos=(-21.675,-15.85,2) rot=(0,0,1;3.14159rad)
  Reference1 = -> Assembly [button_b.Edge17,button_b.Edge17]
  Reference2 = -> Assembly [top_b.Edge111,top_b.Edge111]
FEATURE [Assembly::JointGroup] Joints
  Group = -> [GroundedJoint,Joint,Joint001]
FEATURE [Assembly::AssemblyObject] Assembly
  Group = -> [Joints,bottom_b,GroundedJoint,top_b,button_b,Joint,Joint001]
  Origin = -> Origin006
  Type = Assembly
FEATURE [Sketcher::SketchObject] Sketch021
  ArcFitTolerance = 1e-06
  AttachmentSupport = -> [XY_Plane007]
  FullyConstrained = true
  MakeInternals = false
  MapMode = 5
  sketch-geometry (1):
    g0: Circle CenterX=0 CenterY=0 CenterZ=0 NormalX=0 NormalY=0 NormalZ=1 AngleXU=0 Radius=1.5
  constraints (2):
    c: Diameter(g0) = 3
    c: Coincident(g0,g-1)
FEATURE [PartDesign::Pad] Pad011
  Direction = (0,0,1)
  Length = 3
  Length2 = 10
  Profile = -> Sketch021
  ReferenceAxis = -> Sketch021 [N_Axis]
  Refine = true
  Suppressed = false
  Type = 0
FEATURE [Sketcher::SketchObject] Sketch022
  ArcFitTolerance = 1e-06
  AttachmentSupport = -> [YZ_Plane007]
  ExternalGeometry = -> [Pad011]
  FullyConstrained = true
  MakeInternals = false
  MapMode = 5
  Placement = pos=(0,0,0) rot=(0.57735,0.57735,0.57735;2.0944rad)
  sketch-geometry (7):
    g0: LineSegment StartX=0.5 StartY=4 StartZ=0 EndX=0.5 EndY=2 EndZ=0
    g1: LineSegment StartX=1.5 StartY=3 StartZ=0 EndX=1.65 EndY=3 EndZ=0
    g2: LineSegment StartX=1.65 StartY=3 StartZ=0 EndX=1.65 EndY=3.2 EndZ=0
    g3: LineSegment StartX=1.5 StartY=3 StartZ=0 EndX=1.5 EndY=2 EndZ=0
    g4: LineSegment StartX=1.5 StartY=2 StartZ=0 EndX=0.5 EndY=2 EndZ=0
    g5: LineSegment StartX=0.5 StartY=4 StartZ=0 EndX=0.7 EndY=4 EndZ=0
    g6: LineSegment StartX=0.7 StartY=4 StartZ=0 EndX=1.65 EndY=3.2 EndZ=0
  constraints (20):
    c: Vertical(g0)
    c: Horizontal(g1)
    c: Coincident(g1,g2)
    c: Vertical(g2)
    c: DistanceX(g1,g1) = 0.15
    c: DistanceY(g2,g2) = 0.2
    c: Coincident(g3,g1)
    c: Vertical(g3)
    c: DistanceY(g3,g3) = 1
    c: Coincident(g4,g3)
    c: Horizontal(g4)
    c: Coincident(g4,g0)
    c: DistanceX(g4,g4) = 1
    c: Coincident(g1,g-3)
    c: DistanceY(g0,g0) = 2
    c: Distance(g5) = 0.2
    c: Coincident(g5,g0)
    c: Horizontal(g5)
    c: Coincident(g6,g5)
    c: Coincident(g6,g2)
FEATURE [PartDesign::Revolution] Revolution
  Angle = 360
  Angle2 = 60
  Axis = (0,0,1)
  Base = (0,0,0)
  BaseFeature = -> Pad011
  Profile = -> Sketch022
  ReferenceAxis = -> Sketch022 [V_Axis]
  Refine = true
  Reversed = true
  Suppressed = false
  Type = 0
FEATURE [Sketcher::SketchObject] Sketch023
  ArcFitTolerance = 1e-06
  AttachmentOffset = pos=(0,0,4) rot=(0,0,1;0rad)
  AttachmentSupport = -> [XY_Plane008]
  FullyConstrained = true
  MakeInternals = false
  MapMode = 5
  Placement = pos=(0,0,4) rot=(0,0,1;0rad)
  sketch-geometry (1):
    g0: Circle CenterX=0 CenterY=0 CenterZ=0 NormalX=0 NormalY=0 NormalZ=1 AngleXU=0 Radius=0.5
  constraints (2):
    c: Diameter(g0) = 1
    c: Coincident(g0,g-1)
FEATURE [PartDesign::Pad] Pad012
  Direction = (0,0,1)
  Length = 2
  Length2 = 10
  Profile = -> Sketch023
  ReferenceAxis = -> Sketch023 [N_Axis]
  Refine = true
  Reversed = true
  Suppressed = false
  Type = 0
FEATURE [PartDesign::Body] Body006
  AllowCompound = false
  Group = -> [Sketch023,Pad012]
  Origin = -> Origin008
  Tip = -> Pad012
FEATURE [PartDesign::Boolean] Boolean
  BaseFeature = -> Revolution
  Group = -> [Body006]
  Refine = true
  Suppressed = false
  Type = 1
  UsePlacement = true
FEATURE [Sketcher::SketchObject] Sketch024
  ArcFitTolerance = 1e-06
  AttachmentOffset = pos=(0,0,4) rot=(0,0,1;0rad)
  AttachmentSupport = -> [XY_Plane009]
  FullyConstrained = true
  MakeInternals = false
  MapMode = 5
  Placement = pos=(0,0,4) rot=(0,0,1;0rad)
  sketch-geometry (20):
    g0: LineSegment [constr] StartX=0 StartY=0 StartZ=0 EndX=0.15 EndY=0 EndZ=0
    g1: LineSegment [constr] StartX=0.15 StartY=0 StartZ=0 EndX=0.15 EndY=0.15 EndZ=0
    g2: LineSegment [constr] StartX=0.15 StartY=0.15 StartZ=0 EndX=0 EndY=0.15 EndZ=0
    g3: LineSegment [constr] StartX=0 StartY=0.15 StartZ=0 EndX=0 EndY=0 EndZ=0
    g4: LineSegment [constr] StartX=0 StartY=0 StartZ=0 EndX=-0.15 EndY=0 EndZ=0
    g5: LineSegment [constr] StartX=-0.15 StartY=0 StartZ=0 EndX=-0.15 EndY=-0.15 EndZ=0
    g6: LineSegment [constr] StartX=-0.15 StartY=-0.15 StartZ=0 EndX=0 EndY=-0.15 EndZ=0
    g7: LineSegment [constr] StartX=0 StartY=-0.15 StartZ=0 EndX=0 EndY=0 EndZ=0
    g8: LineSegment StartX=2.15 StartY=0.15 StartZ=0 EndX=0.15 EndY=0.15 EndZ=0
    g9: LineSegment StartX=0.15 StartY=0.15 StartZ=0 EndX=0.15 EndY=2.15 EndZ=0
    g10: LineSegment StartX=0.15 StartY=2.15 StartZ=0 EndX=-0.15 EndY=2.15 EndZ=0
    g11: LineSegment StartX=-0.15 StartY=2.15 StartZ=0 EndX=-0.15 EndY=0.15 EndZ=0
    g12: LineSegment StartX=-0.15 StartY=0.15 StartZ=0 EndX=-2.15 EndY=0.15 EndZ=0
    g13: LineSegment StartX=-2.15 StartY=0.15 StartZ=0 EndX=-2.15 EndY=-0.15 EndZ=0
    g14: LineSegment StartX=-2.15 StartY=-0.15 StartZ=0 EndX=-0.15 EndY=-0.15 EndZ=0
    g15: LineSegment StartX=-0.15 StartY=-0.15 StartZ=0 EndX=-0.15 EndY=-2.15 EndZ=0
    g16: LineSegment StartX=-0.15 StartY=-2.15 StartZ=0 EndX=0.15 EndY=-2.15 EndZ=0
    g17: LineSegment StartX=0.15 StartY=-2.15 StartZ=0 EndX=0.15 EndY=-0.15 EndZ=0
    g18: LineSegment StartX=0.15 StartY=-0.15 StartZ=0 EndX=2.15 EndY=-0.15 EndZ=0
    g19: LineSegment StartX=2.15 StartY=-0.15 StartZ=0 EndX=2.15 EndY=0.15 EndZ=0
  constraints (56):
    c: Coincident(g0,g1)
    c: Coincident(g1,g2)
    c: Coincident(g2,g3)
    c: Coincident(g3,g0)
    c: Horizontal(g0)
    c: Horizontal(g2)
    c: Vertical(g1)
    c: Vertical(g3)
    c: Distance(g1,g3) = 0.15
    c: Distance(g0,g2) = 0.15
    c: Coincident(g0,g-1)
    c: Coincident(g4,g5)
    c: Coincident(g5,g6)
    c: Coincident(g6,g7)
    c: Coincident(g7,g4)
    c: Horizontal(g4)
    c: Horizontal(g6)
    c: Vertical(g5)
    c: Vertical(g7)
    c: Distance(g5,g7) = 0.15
    c: Distance(g4,g6) = 0.15
    c: Coincident(g4,g0)
    c: Coincident(g8,g1)
    c: Horizontal(g8)
    c: Coincident(g8,g9)
    c: Vertical(g9)
    c: Coincident(g9,g10)
    c: Horizontal(g10)
    c: Coincident(g10,g11)
    c: Vertical(g11)
    c: Coincident(g11,g12)
    c: Horizontal(g12)
    c: Coincident(g12,g13)
    c: Coincident(g13,g14)
    c: Horizontal(g14)
    c: Coincident(g14,g15)
    c: Vertical(g15)
    c: Coincident(g15,g16)
    c: Horizontal(g16)
    c: Coincident(g16,g17)
    c: Coincident(g17,g18)
    c: Horizontal(g18)
    c: Coincident(g18,g19)
    c: Coincident(g19,g8)
    c: Vertical(g19)
    c: Vertical(g17)
    c: Vertical(g13)
    c: Distance(g10,g10) = 0.3
    c: DistanceY(g19,g19) = 0.3
    c: DistanceX(g16,g16) = 0.3
    c: DistanceY(g13,g13) = 0.3
    c: Coincident(g5,g14)
    c: DistanceY(g15,g15) = 2
    c: DistanceX(g14,g14) = 2
    c: DistanceX(g8,g8) = 2
    c: DistanceY(g9,g9) = 2
FEATURE [PartDesign::Pad] Pad013
  Direction = (0,0,1)
  Length = 2.5
  Length2 = 10
  Profile = -> Sketch024
  ReferenceAxis = -> Sketch024 [N_Axis]
  Refine = true
  Reversed = true
  Suppressed = false
  Type = 0
FEATURE [PartDesign::Body] Body007
  AllowCompound = false
  Group = -> [Sketch024,Pad013]
  Origin = -> Origin009
  Tip = -> Pad013
FEATURE [PartDesign::Boolean] Boolean001
  BaseFeature = -> Boolean
  Group = -> [Body007]
  Refine = true
  Suppressed = false
  Type = 1
  UsePlacement = true
FEATURE [PartDesign::Body] Body005  label="pcb_holder"
  AllowCompound = false
  Group = -> [Sketch021,Pad011,Sketch022,Revolution,Boolean,Boolean001]
  Origin = -> Origin007
  Placement = pos=(24,0,7) rot=(0,0,1;0rad)
  Tip = -> Boolean001
FEATURE [Sketcher::SketchObject] Sketch025
  ArcFitTolerance = 1e-06
  AttachmentSupport = -> [XY_Plane010]
  FullyConstrained = true
  MakeInternals = false
  MapMode = 5
  sketch-geometry (1):
    g0: Circle CenterX=0 CenterY=0 CenterZ=0 NormalX=0 NormalY=0 NormalZ=1 AngleXU=0 Radius=1.5
  constraints (2):
    c: Diameter(g0) = 3
    c: Coincident(g0,g-1)
FEATURE [PartDesign::Pad] Pad014
  Direction = (0,0,1)
  Length = 3
  Length2 = 10
  Profile = -> Sketch025
  ReferenceAxis = -> Sketch025 [N_Axis]
  Refine = true
  Suppressed = false
  Type = 0
FEATURE [Sketcher::SketchObject] Sketch026
  ArcFitTolerance = 1e-06
  AttachmentSupport = -> [YZ_Plane010]
  ExternalGeometry = -> [Pad014]
  FullyConstrained = true
  MakeInternals = false
  MapMode = 5
  Placement = pos=(0,0,0) rot=(0.57735,0.57735,0.57735;2.0944rad)
  sketch-geometry (7):
    g0: LineSegment StartX=0.5 StartY=4 StartZ=0 EndX=0.5 EndY=2 EndZ=0
    g1: LineSegment StartX=1.5 StartY=3 StartZ=0 EndX=1.65 EndY=3 EndZ=0
    g2: LineSegment StartX=1.65 StartY=3 StartZ=0 EndX=1.65 EndY=3.2 EndZ=0
    g3: LineSegment StartX=1.5 StartY=3 StartZ=0 EndX=1.5 EndY=2 EndZ=0
    g4: LineSegment StartX=1.5 StartY=2 StartZ=0 EndX=0.5 EndY=2 EndZ=0
    g5: LineSegment StartX=0.5 StartY=4 StartZ=0 EndX=0.7 EndY=4 EndZ=0
    g6: LineSegment StartX=0.7 StartY=4 StartZ=0 EndX=1.65 EndY=3.2 EndZ=0
  constraints (20):
    c: Vertical(g0)
    c: Horizontal(g1)
    c: Coincident(g1,g2)
    c: Vertical(g2)
    c: DistanceX(g1,g1) = 0.15
    c: DistanceY(g2,g2) = 0.2
    c: Coincident(g3,g1)
    c: Vertical(g3)
    c: DistanceY(g3,g3) = 1
    c: Coincident(g4,g3)
    c: Horizontal(g4)
    c: Coincident(g4,g0)
    c: DistanceX(g4,g4) = 1
    c: Coincident(g1,g-3)
    c: DistanceY(g0,g0) = 2
    c: Distance(g5) = 0.2
    c: Coincident(g5,g0)
    c: Horizontal(g5)
    c: Coincident(g6,g5)
    c: Coincident(g6,g2)
FEATURE [PartDesign::Revolution] Revolution001
  Angle = 360
  Angle2 = 60
  Axis = (0,0,1)
  Base = (0,0,0)
  BaseFeature = -> Pad014
  Profile = -> Sketch026
  ReferenceAxis = -> Sketch026 [V_Axis]
  Refine = true
  Reversed = true
  Suppressed = false
  Type = 0
FEATURE [Sketcher::SketchObject] Sketch027
  ArcFitTolerance = 1e-06
  AttachmentOffset = pos=(0,0,4) rot=(0,0,1;0rad)
  AttachmentSupport = -> [XY_Plane011]
  FullyConstrained = true
  MakeInternals = false
  MapMode = 5
  Placement = pos=(0,0,4) rot=(0,0,1;0rad)
  sketch-geometry (1):
    g0: Circle CenterX=0 CenterY=0 CenterZ=0 NormalX=0 NormalY=0 NormalZ=1 AngleXU=0 Radius=0.5
  constraints (2):
    c: Diameter(g0) = 1
    c: Coincident(g0,g-1)
FEATURE [PartDesign::Pad] Pad015
  Direction = (0,0,1)
  Length = 2
  Length2 = 10
  Profile = -> Sketch027
  ReferenceAxis = -> Sketch027 [N_Axis]
  Refine = true
  Reversed = true
  Suppressed = false
  Type = 0
FEATURE [PartDesign::Body] Body009
  AllowCompound = false
  Group = -> [Sketch027,Pad015]
  Origin = -> Origin011
  Tip = -> Pad015
FEATURE [PartDesign::Boolean] Boolean002
  BaseFeature = -> Revolution001
  Group = -> [Body009]
  Refine = true
  Suppressed = false
  Type = 1
  UsePlacement = true
FEATURE [Sketcher::SketchObject] Sketch028
  ArcFitTolerance = 1e-06
  AttachmentOffset = pos=(0,0,4) rot=(0,0,1;0rad)
  AttachmentSupport = -> [XY_Plane012]
  FullyConstrained = true
  MakeInternals = false
  MapMode = 5
  Placement = pos=(0,0,4) rot=(0,0,1;0rad)
  sketch-geometry (20):
    g0: LineSegment [constr] StartX=0 StartY=0 StartZ=0 EndX=0.15 EndY=0 EndZ=0
    g1: LineSegment [constr] StartX=0.15 StartY=0 StartZ=0 EndX=0.15 EndY=0.15 EndZ=0
    g2: LineSegment [constr] StartX=0.15 StartY=0.15 StartZ=0 EndX=0 EndY=0.15 EndZ=0
    g3: LineSegment [constr] StartX=0 StartY=0.15 StartZ=0 EndX=0 EndY=0 EndZ=0
    g4: LineSegment [constr] StartX=0 StartY=0 StartZ=0 EndX=-0.15 EndY=0 EndZ=0
    g5: LineSegment [constr] StartX=-0.15 StartY=0 StartZ=0 EndX=-0.15 EndY=-0.15 EndZ=0
    g6: LineSegment [constr] StartX=-0.15 StartY=-0.15 StartZ=0 EndX=0 EndY=-0.15 EndZ=0
    g7: LineSegment [constr] StartX=0 StartY=-0.15 StartZ=0 EndX=0 EndY=0 EndZ=0
    g8: LineSegment StartX=2.15 StartY=0.15 StartZ=0 EndX=0.15 EndY=0.15 EndZ=0
    g9: LineSegment StartX=0.15 StartY=0.15 StartZ=0 EndX=0.15 EndY=2.15 EndZ=0
    g10: LineSegment StartX=0.15 StartY=2.15 StartZ=0 EndX=-0.15 EndY=2.15 EndZ=0
    g11: LineSegment StartX=-0.15 StartY=2.15 StartZ=0 EndX=-0.15 EndY=0.15 EndZ=0
    g12: LineSegment StartX=-0.15 StartY=0.15 StartZ=0 EndX=-2.15 EndY=0.15 EndZ=0
    g13: LineSegment StartX=-2.15 StartY=0.15 StartZ=0 EndX=-2.15 EndY=-0.15 EndZ=0
    g14: LineSegment StartX=-2.15 StartY=-0.15 StartZ=0 EndX=-0.15 EndY=-0.15 EndZ=0
    g15: LineSegment StartX=-0.15 StartY=-0.15 StartZ=0 EndX=-0.15 EndY=-2.15 EndZ=0
    g16: LineSegment StartX=-0.15 StartY=-2.15 StartZ=0 EndX=0.15 EndY=-2.15 EndZ=0
    g17: LineSegment StartX=0.15 StartY=-2.15 StartZ=0 EndX=0.15 EndY=-0.15 EndZ=0
    g18: LineSegment StartX=0.15 StartY=-0.15 StartZ=0 EndX=2.15 EndY=-0.15 EndZ=0
    g19: LineSegment StartX=2.15 StartY=-0.15 StartZ=0 EndX=2.15 EndY=0.15 EndZ=0
  constraints (56):
    c: Coincident(g0,g1)
    c: Coincident(g1,g2)
    c: Coincident(g2,g3)
    c: Coincident(g3,g0)
    c: Horizontal(g0)
    c: Horizontal(g2)
    c: Vertical(g1)
    c: Vertical(g3)
    c: Distance(g1,g3) = 0.15
    c: Distance(g0,g2) = 0.15
    c: Coincident(g0,g-1)
    c: Coincident(g4,g5)
    c: Coincident(g5,g6)
    c: Coincident(g6,g7)
    c: Coincident(g7,g4)
    c: Horizontal(g4)
    c: Horizontal(g6)
    c: Vertical(g5)
    c: Vertical(g7)
    c: Distance(g5,g7) = 0.15
    c: Distance(g4,g6) = 0.15
    c: Coincident(g4,g0)
    c: Coincident(g8,g1)
    c: Horizontal(g8)
    c: Coincident(g8,g9)
    c: Vertical(g9)
    c: Coincident(g9,g10)
    c: Horizontal(g10)
    c: Coincident(g10,g11)
    c: Vertical(g11)
    c: Coincident(g11,g12)
    c: Horizontal(g12)
    c: Coincident(g12,g13)
    c: Coincident(g13,g14)
    c: Horizontal(g14)
    c: Coincident(g14,g15)
    c: Vertical(g15)
    c: Coincident(g15,g16)
    c: Horizontal(g16)
    c: Coincident(g16,g17)
    c: Coincident(g17,g18)
    c: Horizontal(g18)
    c: Coincident(g18,g19)
    c: Coincident(g19,g8)
    c: Vertical(g19)
    c: Vertical(g17)
    c: Vertical(g13)
    c: Distance(g10,g10) = 0.3
    c: DistanceY(g19,g19) = 0.3
    c: DistanceX(g16,g16) = 0.3
    c: DistanceY(g13,g13) = 0.3
    c: Coincident(g5,g14)
    c: DistanceY(g15,g15) = 2
    c: DistanceX(g14,g14) = 2
    c: DistanceX(g8,g8) = 2
    c: DistanceY(g9,g9) = 2
FEATURE [PartDesign::Pad] Pad016
  Direction = (0,0,1)
  Length = 2.5
  Length2 = 10
  Profile = -> Sketch028
  ReferenceAxis = -> Sketch028 [N_Axis]
  Refine = true
  Reversed = true
  Suppressed = false
  Type = 0
FEATURE [PartDesign::Body] Body010
  AllowCompound = false
  Group = -> [Sketch028,Pad016]
  Origin = -> Origin012
  Tip = -> Pad016
FEATURE [PartDesign::Boolean] Boolean003
  BaseFeature = -> Boolean002
  Group = -> [Body010]
  Refine = true
  Suppressed = false
  Type = 1
  UsePlacement = true
FEATURE [PartDesign::Body] Body008  label="pcb_holder001"
  AllowCompound = false
  Group = -> [Sketch025,Pad014,Sketch026,Revolution001,Boolean002,Boolean003]
  Origin = -> Origin010
  Placement = pos=(-28,-23,7) rot=(0,0,1;0rad)
  Tip = -> Boolean003
FEATURE [Sketcher::SketchObject] Sketch029
  ArcFitTolerance = 1e-06
  AttachmentSupport = -> [XY_Plane013]
  FullyConstrained = true
  MakeInternals = false
  MapMode = 5
  sketch-geometry (1):
    g0: Circle CenterX=0 CenterY=0 CenterZ=0 NormalX=0 NormalY=0 NormalZ=1 AngleXU=0 Radius=1.5
  constraints (2):
    c: Diameter(g0) = 3
    c: Coincident(g0,g-1)
FEATURE [PartDesign::Pad] Pad017
  Direction = (0,0,1)
  Length = 3
  Length2 = 10
  Profile = -> Sketch029
  ReferenceAxis = -> Sketch029 [N_Axis]
  Refine = true
  Suppressed = false
  Type = 0
FEATURE [Sketcher::SketchObject] Sketch030
  ArcFitTolerance = 1e-06
  AttachmentSupport = -> [YZ_Plane013]
  ExternalGeometry = -> [Pad017]
  FullyConstrained = true
  MakeInternals = false
  MapMode = 5
  Placement = pos=(0,0,0) rot=(0.57735,0.57735,0.57735;2.0944rad)
  sketch-geometry (7):
    g0: LineSegment StartX=0.5 StartY=4 StartZ=0 EndX=0.5 EndY=2 EndZ=0
    g1: LineSegment StartX=1.5 StartY=3 StartZ=0 EndX=1.65 EndY=3 EndZ=0
    g2: LineSegment StartX=1.65 StartY=3 StartZ=0 EndX=1.65 EndY=3.2 EndZ=0
    g3: LineSegment StartX=1.5 StartY=3 StartZ=0 EndX=1.5 EndY=2 EndZ=0
    g4: LineSegment StartX=1.5 StartY=2 StartZ=0 EndX=0.5 EndY=2 EndZ=0
    g5: LineSegment StartX=0.5 StartY=4 StartZ=0 EndX=0.7 EndY=4 EndZ=0
    g6: LineSegment StartX=0.7 StartY=4 StartZ=0 EndX=1.65 EndY=3.2 EndZ=0
  constraints (20):
    c: Vertical(g0)
    c: Horizontal(g1)
    c: Coincident(g1,g2)
    c: Vertical(g2)
    c: DistanceX(g1,g1) = 0.15
    c: DistanceY(g2,g2) = 0.2
    c: Coincident(g3,g1)
    c: Vertical(g3)
    c: DistanceY(g3,g3) = 1
    c: Coincident(g4,g3)
    c: Horizontal(g4)
    c: Coincident(g4,g0)
    c: DistanceX(g4,g4) = 1
    c: Coincident(g1,g-3)
    c: DistanceY(g0,g0) = 2
    c: Distance(g5) = 0.2
    c: Coincident(g5,g0)
    c: Horizontal(g5)
    c: Coincident(g6,g5)
    c: Coincident(g6,g2)
FEATURE [PartDesign::Revolution] Revolution002
  Angle = 360
  Angle2 = 60
  Axis = (0,0,1)
  Base = (0,0,0)
  BaseFeature = -> Pad017
  Profile = -> Sketch030
  ReferenceAxis = -> Sketch030 [V_Axis]
  Refine = true
  Reversed = true
  Suppressed = false
  Type = 0
FEATURE [Sketcher::SketchObject] Sketch031
  ArcFitTolerance = 1e-06
  AttachmentOffset = pos=(0,0,4) rot=(0,0,1;0rad)
  AttachmentSupport = -> [XY_Plane014]
  FullyConstrained = true
  MakeInternals = false
  MapMode = 5
  Placement = pos=(0,0,4) rot=(0,0,1;0rad)
  sketch-geometry (1):
    g0: Circle CenterX=0 CenterY=0 CenterZ=0 NormalX=0 NormalY=0 NormalZ=1 AngleXU=0 Radius=0.5
  constraints (2):
    c: Diameter(g0) = 1
    c: Coincident(g0,g-1)
FEATURE [PartDesign::Pad] Pad018
  Direction = (0,0,1)
  Length = 2
  Length2 = 10
  Profile = -> Sketch031
  ReferenceAxis = -> Sketch031 [N_Axis]
  Refine = true
  Reversed = true
  Suppressed = false
  Type = 0
FEATURE [PartDesign::Body] Body012
  AllowCompound = false
  Group = -> [Sketch031,Pad018]
  Origin = -> Origin014
  Tip = -> Pad018
FEATURE [PartDesign::Boolean] Boolean004
  BaseFeature = -> Revolution002
  Group = -> [Body012]
  Refine = true
  Suppressed = false
  Type = 1
  UsePlacement = true
FEATURE [Sketcher::SketchObject] Sketch032
  ArcFitTolerance = 1e-06
  AttachmentOffset = pos=(0,0,4) rot=(0,0,1;0rad)
  AttachmentSupport = -> [XY_Plane015]
  FullyConstrained = true
  MakeInternals = false
  MapMode = 5
  Placement = pos=(0,0,4) rot=(0,0,1;0rad)
  sketch-geometry (20):
    g0: LineSegment [constr] StartX=0 StartY=0 StartZ=0 EndX=0.15 EndY=0 EndZ=0
    g1: LineSegment [constr] StartX=0.15 StartY=0 StartZ=0 EndX=0.15 EndY=0.15 EndZ=0
    g2: LineSegment [constr] StartX=0.15 StartY=0.15 StartZ=0 EndX=0 EndY=0.15 EndZ=0
    g3: LineSegment [constr] StartX=0 StartY=0.15 StartZ=0 EndX=0 EndY=0 EndZ=0
    g4: LineSegment [constr] StartX=0 StartY=0 StartZ=0 EndX=-0.15 EndY=0 EndZ=0
    g5: LineSegment [constr] StartX=-0.15 StartY=0 StartZ=0 EndX=-0.15 EndY=-0.15 EndZ=0
    g6: LineSegment [constr] StartX=-0.15 StartY=-0.15 StartZ=0 EndX=0 EndY=-0.15 EndZ=0
    g7: LineSegment [constr] StartX=0 StartY=-0.15 StartZ=0 EndX=0 EndY=0 EndZ=0
    g8: LineSegment StartX=2.15 StartY=0.15 StartZ=0 EndX=0.15 EndY=0.15 EndZ=0
    g9: LineSegment StartX=0.15 StartY=0.15 StartZ=0 EndX=0.15 EndY=2.15 EndZ=0
    g10: LineSegment StartX=0.15 StartY=2.15 StartZ=0 EndX=-0.15 EndY=2.15 EndZ=0
    g11: LineSegment StartX=-0.15 StartY=2.15 StartZ=0 EndX=-0.15 EndY=0.15 EndZ=0
    g12: LineSegment StartX=-0.15 StartY=0.15 StartZ=0 EndX=-2.15 EndY=0.15 EndZ=0
    g13: LineSegment StartX=-2.15 StartY=0.15 StartZ=0 EndX=-2.15 EndY=-0.15 EndZ=0
    g14: LineSegment StartX=-2.15 StartY=-0.15 StartZ=0 EndX=-0.15 EndY=-0.15 EndZ=0
    g15: LineSegment StartX=-0.15 StartY=-0.15 StartZ=0 EndX=-0.15 EndY=-2.15 EndZ=0
    g16: LineSegment StartX=-0.15 StartY=-2.15 StartZ=0 EndX=0.15 EndY=-2.15 EndZ=0
    g17: LineSegment StartX=0.15 StartY=-2.15 StartZ=0 EndX=0.15 EndY=-0.15 EndZ=0
    g18: LineSegment StartX=0.15 StartY=-0.15 StartZ=0 EndX=2.15 EndY=-0.15 EndZ=0
    g19: LineSegment StartX=2.15 StartY=-0.15 StartZ=0 EndX=2.15 EndY=0.15 EndZ=0
  constraints (56):
    c: Coincident(g0,g1)
    c: Coincident(g1,g2)
    c: Coincident(g2,g3)
    c: Coincident(g3,g0)
    c: Horizontal(g0)
    c: Horizontal(g2)
    c: Vertical(g1)
    c: Vertical(g3)
    c: Distance(g1,g3) = 0.15
    c: Distance(g0,g2) = 0.15
    c: Coincident(g0,g-1)
    c: Coincident(g4,g5)
    c: Coincident(g5,g6)
    c: Coincident(g6,g7)
    c: Coincident(g7,g4)
    c: Horizontal(g4)
    c: Horizontal(g6)
    c: Vertical(g5)
    c: Vertical(g7)
    c: Distance(g5,g7) = 0.15
    c: Distance(g4,g6) = 0.15
    c: Coincident(g4,g0)
    c: Coincident(g8,g1)
    c: Horizontal(g8)
    c: Coincident(g8,g9)
    c: Vertical(g9)
    c: Coincident(g9,g10)
    c: Horizontal(g10)
    c: Coincident(g10,g11)
    c: Vertical(g11)
    c: Coincident(g11,g12)
    c: Horizontal(g12)
    c: Coincident(g12,g13)
    c: Coincident(g13,g14)
    c: Horizontal(g14)
    c: Coincident(g14,g15)
    c: Vertical(g15)
    c: Coincident(g15,g16)
    c: Horizontal(g16)
    c: Coincident(g16,g17)
    c: Coincident(g17,g18)
    c: Horizontal(g18)
    c: Coincident(g18,g19)
    c: Coincident(g19,g8)
    c: Vertical(g19)
    c: Vertical(g17)
    c: Vertical(g13)
    c: Distance(g10,g10) = 0.3
    c: DistanceY(g19,g19) = 0.3
    c: DistanceX(g16,g16) = 0.3
    c: DistanceY(g13,g13) = 0.3
    c: Coincident(g5,g14)
    c: DistanceY(g15,g15) = 2
    c: DistanceX(g14,g14) = 2
    c: DistanceX(g8,g8) = 2
    c: DistanceY(g9,g9) = 2
FEATURE [PartDesign::Pad] Pad019
  Direction = (0,0,1)
  Length = 2.5
  Length2 = 10
  Profile = -> Sketch032
  ReferenceAxis = -> Sketch032 [N_Axis]
  Refine = true
  Reversed = true
  Suppressed = false
  Type = 0
FEATURE [PartDesign::Body] Body013
  AllowCompound = false
  Group = -> [Sketch032,Pad019]
  Origin = -> Origin015
  Tip = -> Pad019
FEATURE [PartDesign::Boolean] Boolean005
  BaseFeature = -> Boolean004
  Group = -> [Body013]
  Refine = true
  Suppressed = false
  Type = 1
  UsePlacement = true
FEATURE [PartDesign::Body] Body011  label="pcb_holder002"
  AllowCompound = false
  Group = -> [Sketch029,Pad017,Sketch030,Revolution002,Boolean004,Boolean005]
  Origin = -> Origin013
  Placement = pos=(-28,16,7) rot=(0,0,1;0rad)
  Tip = -> Boolean005
FEATURE [PartDesign::Boolean] Boolean006
  BaseFeature = -> Pocket008
  Group = -> [Body005]
  Refine = true
  Suppressed = false
  Type = 0
  UsePlacement = true
FEATURE [PartDesign::Boolean] Boolean007
  BaseFeature = -> Boolean006
  Group = -> [Body008,Body011]
  Refine = true
  Suppressed = false
  Type = 0
  UsePlacement = true
FEATURE [PartDesign::Body] Body  label="bottom_b"
  AllowCompound = false
  Group = -> [Sketch,Pad,Thickness,Fillet,Sketch001,Pad001,Fillet001,Sketch003,Pocket,Sketch004,Pocket001,Sketch016,Sketch018,Pad009,Fillet004,Pocket007,Sketch019,Pocket008,Boolean006,Boolean007]
  Origin = -> Origin001
  Tip = -> Boolean007
FEATURE [Sketcher::SketchObject] Sketch033
  ArcFitTolerance = 1e-06
  AttachmentSupport = -> [XY_Plane002]
  ExternalGeometry = -> [Pad010]
  FullyConstrained = true
  MakeInternals = false
  MapMode = 5
  sketch-geometry (13):
    g0: LineSegment [constr] StartX=-16 StartY=-19.7 StartZ=0 EndX=-16 EndY=-27.7 EndZ=0
    g1: LineSegment [constr] StartX=-16 StartY=-27.7 StartZ=0 EndX=-14 EndY=-27.7 EndZ=0
    g2: LineSegment [constr] StartX=-14 StartY=-27.7 StartZ=0 EndX=-14 EndY=-19.7 EndZ=0
    g3: LineSegment [constr] StartX=-14 StartY=-19.7 StartZ=0 EndX=-16 EndY=-19.7 EndZ=0
    g4: LineSegment StartX=-14 StartY=-19.7 StartZ=0 EndX=-14 EndY=-27.7 EndZ=0
    g5: LineSegment StartX=-14 StartY=-27.7 StartZ=0 EndX=-12 EndY=-27.7 EndZ=0
    g6: LineSegment StartX=-12 StartY=-27.7 StartZ=0 EndX=-12 EndY=-19.7 EndZ=0
    g7: LineSegment StartX=-12 StartY=-19.7 StartZ=0 EndX=-14 EndY=-19.7 EndZ=0
    g8: LineSegment [constr] StartX=-12 StartY=-19.7 StartZ=0 EndX=-6 EndY=-19.7 EndZ=0
    g9: LineSegment StartX=-6 StartY=-19.7 StartZ=0 EndX=-6 EndY=-27.7 EndZ=0
    g10: LineSegment StartX=-6 StartY=-27.7 StartZ=0 EndX=-4 EndY=-27.7 EndZ=0
    g11: LineSegment StartX=-4 StartY=-27.7 StartZ=0 EndX=-4 EndY=-19.7 EndZ=0
    g12: LineSegment StartX=-4 StartY=-19.7 StartZ=0 EndX=-6 EndY=-19.7 EndZ=0
  constraints (36):
    c: Coincident(g0,g1)
    c: Coincident(g1,g2)
    c: Coincident(g2,g3)
    c: Coincident(g3,g0)
    c: Vertical(g0)
    c: Vertical(g2)
    c: Horizontal(g1)
    c: Horizontal(g3)
    c: Distance(g0,g2) = 2
    c: Distance(g1,g3) = 8
    c: Coincident(g0,g-3)
    c: Coincident(g4,g5)
    c: Coincident(g5,g6)
    c: Coincident(g6,g7)
    c: Coincident(g7,g4)
    c: Vertical(g4)
    c: Vertical(g6)
    c: Horizontal(g5)
    c: Horizontal(g7)
    c: Distance(g4,g6) = 2
    c: Distance(g5,g7) = 8
    c: Coincident(g4,g2)
    c: Distance(g8) = 6
    c: Coincident(g8,g6)
    c: Horizontal(g8)
    c: Coincident(g9,g10)
    c: Coincident(g10,g11)
    c: Coincident(g11,g12)
    c: Coincident(g12,g9)
    c: Vertical(g9)
    c: Vertical(g11)
    c: Horizontal(g10)
    c: Horizontal(g12)
    c: Distance(g9,g11) = 2
    c: Distance(g10,g12) = 8
    c: Coincident(g9,g8)
FEATURE [PartDesign::Pad] Pad020  label="cable_clips_bottom"
  BaseFeature = -> Pad010
  Direction = (0,0,1)
  Length = 2
  Length2 = 10
  Profile = -> Sketch033
  ReferenceAxis = -> Sketch033 [N_Axis]
  Refine = true
  Reversed = true
  Suppressed = false
  Type = 0
FEATURE [PartDesign::Fillet] Fillet005  label="cable_clips_f"
  Base = -> Pad020 [Edge98,Edge82,Edge101,Edge85]
  BaseFeature = -> Pad020
  Radius = 1
  Refine = true
  SupportTransform = false
  Suppressed = false
  UseAllEdges = false
FEATURE [Sketcher::SketchObject] Sketch034
  ArcFitTolerance = 1e-06
  AttachmentOffset = pos=(0,0,-2) rot=(0,0,1;0rad)
  AttachmentSupport = -> [XY_Plane002]
  ExternalGeometry = -> [Sketch033]
  FullyConstrained = true
  MakeInternals = false
  MapMode = 5
  Placement = pos=(0,0,-2) rot=(0,0,1;0rad)
  sketch-geometry (5):
    g0: LineSegment [constr] StartX=-12 StartY=-19.7 StartZ=0 EndX=-10 EndY=-19.7 EndZ=0
    g1: LineSegment StartX=-10 StartY=-19.7 StartZ=0 EndX=-10 EndY=-27.7 EndZ=0
    g2: LineSegment StartX=-10 StartY=-27.7 StartZ=0 EndX=-8 EndY=-27.7 EndZ=0
    g3: LineSegment StartX=-8 StartY=-27.7 StartZ=0 EndX=-8 EndY=-19.7 EndZ=0
    g4: LineSegment StartX=-8 StartY=-19.7 StartZ=0 EndX=-10 EndY=-19.7 EndZ=0
  constraints (14):
    c: Distance(g0) = 2
    c: Coincident(g0,g-3)
    c: Horizontal(g0)
    c: Coincident(g1,g2)
    c: Coincident(g2,g3)
    c: Coincident(g3,g4)
    c: Coincident(g4,g1)
    c: Vertical(g1)
    c: Vertical(g3)
    c: Horizontal(g2)
    c: Horizontal(g4)
    c: Distance(g1,g3) = 2
    c: Distance(g2,g4) = 8
    c: Coincident(g1,g0)
FEATURE [Sketcher::SketchObject] Sketch035
  ArcFitTolerance = 1e-06
  AttachmentSupport = -> [XY_Plane002]
  ExternalGeometry = -> [Sketch033]
  FullyConstrained = true
  MakeInternals = false
  MapMode = 5
  sketch-geometry (5):
    g0: LineSegment [constr] StartX=-12 StartY=-19.7 StartZ=0 EndX=-10 EndY=-19.7 EndZ=0
    g1: LineSegment StartX=-10 StartY=-19.7 StartZ=0 EndX=-10 EndY=-21.7 EndZ=0
    g2: LineSegment StartX=-10 StartY=-21.7 StartZ=0 EndX=-8 EndY=-21.7 EndZ=0
    g3: LineSegment StartX=-8 StartY=-21.7 StartZ=0 EndX=-8 EndY=-19.7 EndZ=0
    g4: LineSegment StartX=-8 StartY=-19.7 StartZ=0 EndX=-10 EndY=-19.7 EndZ=0
  constraints (14):
    c: Distance(g0) = 2
    c: Coincident(g0,g-3)
    c: Horizontal(g0)
    c: Coincident(g1,g2)
    c: Coincident(g2,g3)
    c: Coincident(g3,g4)
    c: Coincident(g4,g1)
    c: Vertical(g1)
    c: Vertical(g3)
    c: Horizontal(g2)
    c: Horizontal(g4)
    c: Distance(g1,g3) = 2
    c: Distance(g2,g4) = 2
    c: Coincident(g1,g0)
FEATURE [PartDesign::Pad] Pad022  label="cable_clip_top_holder"
  BaseFeature = -> Fillet005
  Direction = (0,0,1)
  Length = 2.5
  Length2 = 10
  Profile = -> Sketch035
  ReferenceAxis = -> Sketch035 [N_Axis]
  Refine = true
  Reversed = true
  Suppressed = false
  Type = 0
FEATURE [PartDesign::Pad] Pad023  label="cable_clip_top"
  BaseFeature = -> Pad022
  Direction = (0,0,1)
  Length = 2
  Length2 = 10
  Profile = -> Sketch034
  ReferenceAxis = -> Sketch034 [N_Axis]
  Refine = true
  Reversed = true
  Suppressed = false
  Type = 0
FEATURE [PartDesign::Fillet] Fillet006
  Base = -> Pad023 [Edge177,Edge174,Edge148]
  BaseFeature = -> Pad023
  Radius = 0.9
  Refine = true
  SupportTransform = false
  Suppressed = false
  UseAllEdges = false
FEATURE [PartDesign::Body] Body001  label="top_b"
  AllowCompound = false
  Group = -> [Sketch005,Pad003,Thickness001,Fillet002,Sketch008,Pocket002,Sketch009,Pocket004,Sketch020,Pad010,Sketch033,Pad020,Fillet005,Sketch034,Sketch035,Pad022,Pad023,Fillet006]
  Origin = -> Origin002
  Placement = pos=(90,0,0) rot=(0,0,1;0rad)
  Tip = -> Fillet006
FEATURE [App::Part] Part
  Group = -> [Body,Body001,Body004]
  Origin = -> Origin
